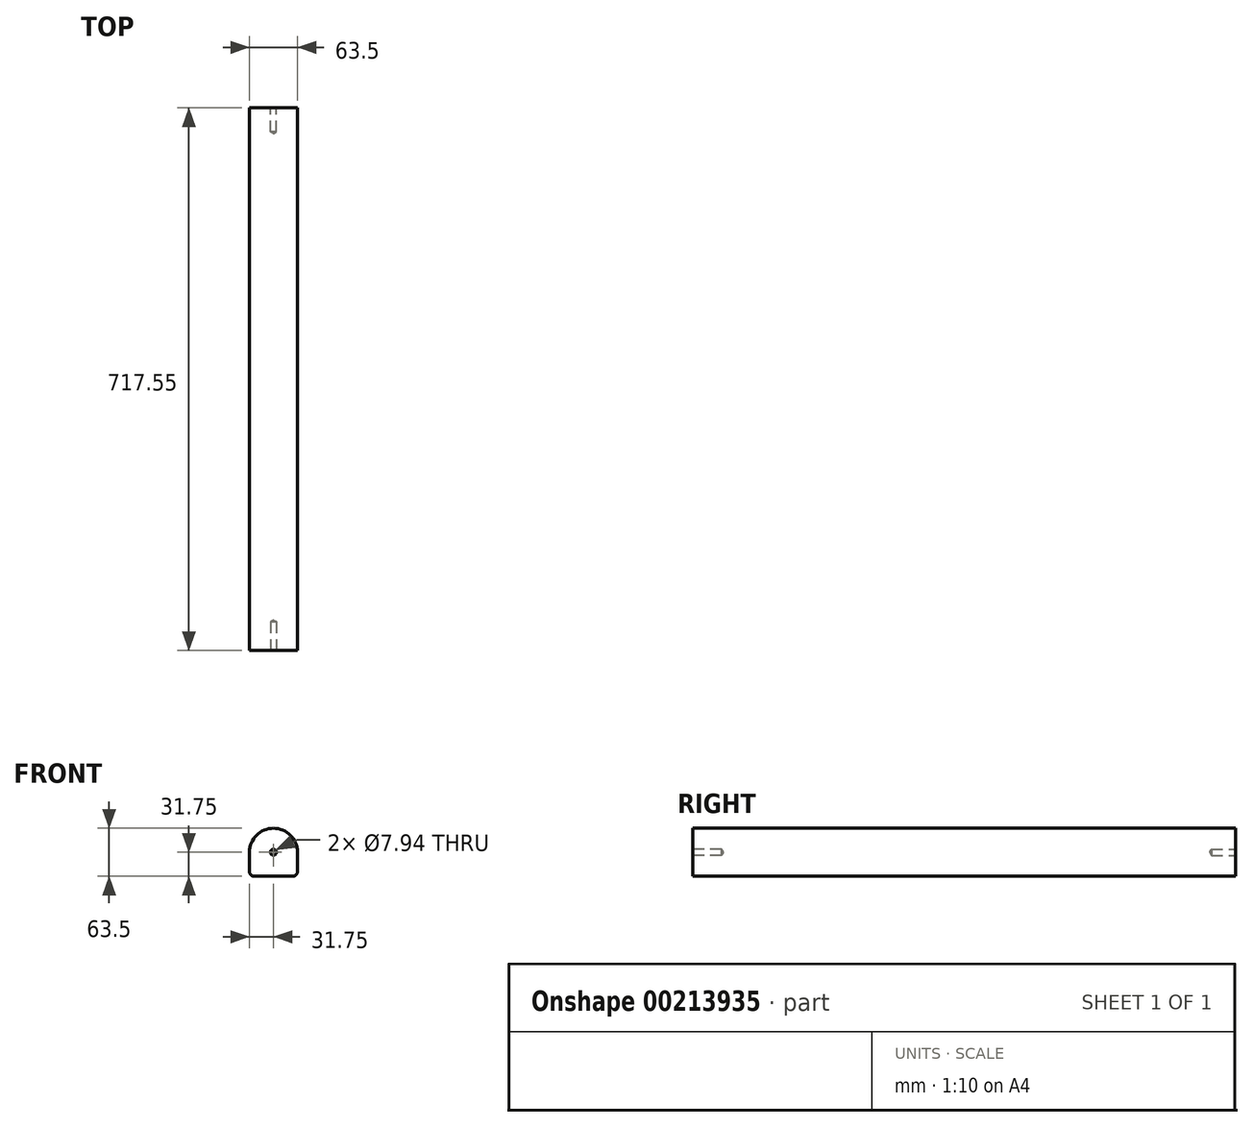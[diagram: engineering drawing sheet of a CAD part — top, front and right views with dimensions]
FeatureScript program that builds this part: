
annotation { "Feature Type Name" : "Feature", "Feature Type Description" : "" }
export const myFeature = defineFeature(function(context is Context, id is Id, definition is map)
    precondition{}
    {
        {
            var Q0;
            Q0=qCreatedBy(makeId("Front.planeOp"),FACE);
            var sketch = newSketch(context, id + "F0", { "sketchPlane" : qUnion([Q0])});
            skLineSegment(sketch, "E0", {"start": v(6.35, 0) * mm, "end": v(57.15, 0) * mm});
            skLineSegment(sketch, "E1", {"start": v(0, 6.35) * mm, "end": v(0, 31.75) * mm});
            skLineSegment(sketch, "E2", {"start": v(63.5, 6.35) * mm, "end": v(63.5, 31.75) * mm});
            skArc(sketch, "E3", {"start": v(0, 31.75) * mm, "mid": v(31.75, 63.5) * mm, "end": v(63.5, 31.75) * mm});
            skPoint(sketch, "E3.centerSnap0", {"position": v(31.75, 0) * mm});
            skPoint(sketch, "E4.visualSharp", {"position": v(0, 0) * mm});
            skArc(sketch, "E4.filletArc", {"start": v(0, 6.35) * mm, "mid": v(1.86, 1.86) * mm, "end": v(6.35, 0) * mm});
            skPoint(sketch, "E5.visualSharp", {"position": v(63.5, 0) * mm});
            skArc(sketch, "E5.filletArc", {"start": v(57.15, 0) * mm, "mid": v(61.64, 1.86) * mm, "end": v(63.5, 6.35) * mm});
            skSolve(sketch);
        }
        {
            var Q0;
            Q0 = qSketchRegion(id + "F0", true);
            extrude(context, id + "F1", {"entities" : qUnion([Q0]), "flatOperationType" : FlatOperationType.REMOVE, "offsetDistance" : 25.4 * mm, "depth" : 717.55 * mm, "domain" : OperationDomain.MODEL});
        }
        {
            var Q0;
            Q0=makeQuery(id+"F1.opExtrude","CAP_FACE",FACE,{"disambiguationData":[OSD([sQuery(id+"F0.wireOp",EDGE,"E0"),sQuery(id+"F0.wireOp",EDGE,"E1"),sQuery(id+"F0.wireOp",EDGE,"E2"),sQuery(id+"F0.wireOp",EDGE,"E3"),sQuery(id+"F0.wireOp",EDGE,"E4.filletArc"),sQuery(id+"F0.wireOp",EDGE,"E5.filletArc")])],"isStart":false});
            var sketch = newSketch(context, id + "F2", { "sketchPlane" : qUnion([Q0])});
            skPoint(sketch, "E6", {"position": v(31.75, 31.75) * mm});
            skSolve(sketch);
        }
        {
            var Q0;
            Q0=sQuery(id+"F2.wireOp",VERTEX,"E6");
            var Q1;
            Q1=makeQuery(id+"F1.opExtrude","SWEPT_BODY",BODY,{"disambiguationData":[OSD([sQuery(id+"F0.wireOp",EDGE,"E0"),sQuery(id+"F0.wireOp",EDGE,"E1"),sQuery(id+"F0.wireOp",EDGE,"E2"),sQuery(id+"F0.wireOp",EDGE,"E3"),sQuery(id+"F0.wireOp",EDGE,"E4.filletArc"),sQuery(id+"F0.wireOp",EDGE,"E5.filletArc")])]});
            hole(context, id + "F3", {"style" : HoleStyle.SIMPLE, "endStyle" : HoleEndStyle.BLIND, "standardTappedOrClearance" : lookupTablePath({ "standard" : "ANSI", "engagement" : "75%", "pitch" : "16 tpi", "size" : "3/8", "type" : "Tapped" }), "standardBlindInLast" : lookupTablePath({ "standard" : "ANSI", "engagement" : "75%", "pitch" : "16 tpi", "size" : "3/8", "type" : "Tapped" }), "holeDiameter" : 7.94 * mm, "holeDepth" : 38.1 * mm, "startFromSketch" : true, "locations" : qUnion([Q0]), "scope" : qUnion([Q1]), "tappedDepth" : 33.34 * mm, "tapClearance" : 3, "majorDiameter" : 9.53 * mm, "showTappedDepth" : true});
        }
        {
            var Q0;
            Q0=makeQuery(id+"F1.opExtrude","CAP_FACE",FACE,{"disambiguationData":[OSD([sQuery(id+"F0.wireOp",EDGE,"E0"),sQuery(id+"F0.wireOp",EDGE,"E1"),sQuery(id+"F0.wireOp",EDGE,"E2"),sQuery(id+"F0.wireOp",EDGE,"E3"),sQuery(id+"F0.wireOp",EDGE,"E4.filletArc"),sQuery(id+"F0.wireOp",EDGE,"E5.filletArc")])],"isStart":true});
            var sketch = newSketch(context, id + "F4", { "sketchPlane" : qUnion([Q0])});
            skPoint(sketch, "E7", {"position": v(-31.75, 31.75) * mm});
            skSolve(sketch);
        }
        {
            var Q0;
            Q0=sQuery(id+"F4.wireOp",VERTEX,"E7");
            var Q1;
            Q1=makeQuery(id+"F1.opExtrude","SWEPT_BODY",BODY,{"disambiguationData":[OSD([sQuery(id+"F0.wireOp",EDGE,"E0"),sQuery(id+"F0.wireOp",EDGE,"E1"),sQuery(id+"F0.wireOp",EDGE,"E2"),sQuery(id+"F0.wireOp",EDGE,"E3"),sQuery(id+"F0.wireOp",EDGE,"E4.filletArc"),sQuery(id+"F0.wireOp",EDGE,"E5.filletArc")])]});
            hole(context, id + "F5", {"style" : HoleStyle.SIMPLE, "endStyle" : HoleEndStyle.BLIND, "standardTappedOrClearance" : lookupTablePath({ "standard" : "ANSI", "engagement" : "75%", "pitch" : "16 tpi", "size" : "3/8", "type" : "Tapped" }), "standardBlindInLast" : lookupTablePath({ "standard" : "ANSI", "engagement" : "75%", "pitch" : "16 tpi", "size" : "3/8", "type" : "Tapped" }), "holeDiameter" : 7.94 * mm, "holeDepth" : 31.75 * mm, "startFromSketch" : true, "locations" : qUnion([Q0]), "scope" : qUnion([Q1]), "tappedDepth" : 12.7 * mm, "tapClearance" : 3, "majorDiameter" : 9.53 * mm});
        }
    });
